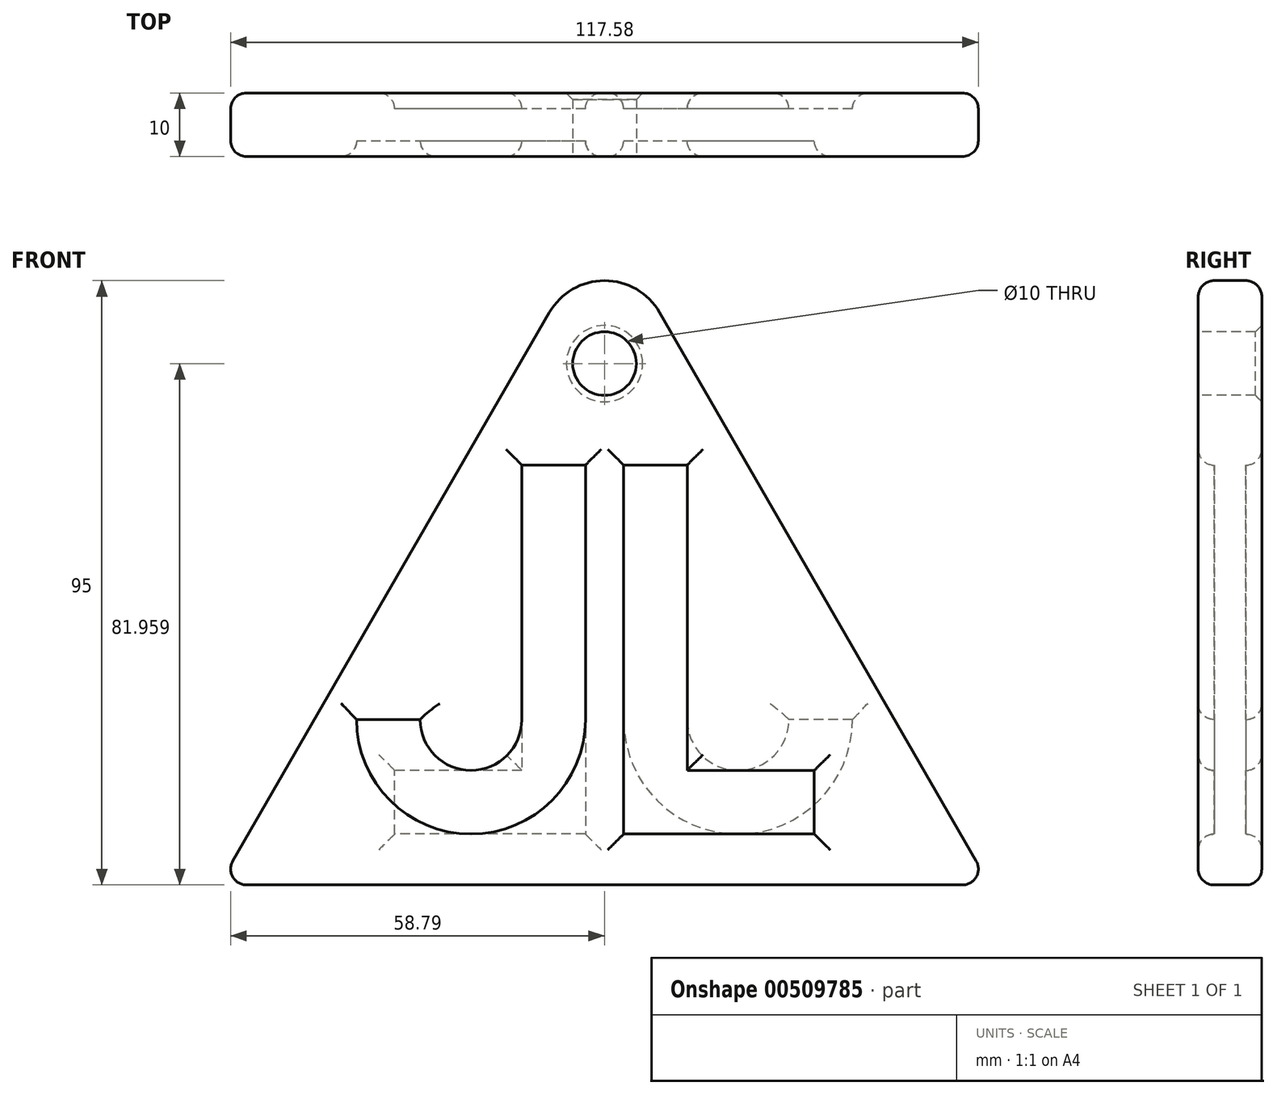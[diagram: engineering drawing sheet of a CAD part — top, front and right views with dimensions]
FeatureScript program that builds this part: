
annotation { "Feature Type Name" : "Feature", "Feature Type Description" : "" }
export const myFeature = defineFeature(function(context is Context, id is Id, definition is map)
    precondition{}
    {
        {
            var Q0;
            Q0=qCreatedBy(makeId("Front.planeOp"),FACE);
            var sketch = newSketch(context, id + "F0", { "sketchPlane" : qUnion([Q0])});
            skCircle(sketch, "E0.cCircle", {"center": v(0, 0) * mm, "radius": 35 * mm, "construction": true});
            skLineSegment(sketch, "E0.0", {"start": v(0, 70) * mm, "end": v(60.62, -35) * mm});
            skLineSegment(sketch, "E0.1", {"start": v(60.62, -35) * mm, "end": v(-60.62, -35) * mm});
            skLineSegment(sketch, "E0.2", {"start": v(-60.62, -35) * mm, "end": v(0, 70) * mm});
            skPoint(sketch, "E0.0.midPoint", {"position": v(30.31, 17.5) * mm});
            skSolve(sketch);
        }
        {
            var Q0;
            Q0=qCreatedBy(makeId("Front.planeOp"),FACE);
            var sketch = newSketch(context, id + "F1", { "sketchPlane" : qUnion([Q0])});
            skLineSegment(sketch, "E1.left", {"start": v(-3, -9) * mm, "end": v(-3, 31) * mm});
            skArc(sketch, "E2", {"start": v(-3, -9) * mm, "mid": v(-21, -27) * mm, "end": v(-39, -9) * mm});
            skArc(sketch, "E3", {"start": v(-13, -9) * mm, "mid": v(-21, -17) * mm, "end": v(-29, -9) * mm});
            skLineSegment(sketch, "E4.top", {"start": v(-13, 31) * mm, "end": v(-3, 31) * mm});
            skLineSegment(sketch, "E4.left", {"start": v(-13, -9) * mm, "end": v(-13, 31) * mm});
            skLineSegment(sketch, "E5", {"start": v(-39, -9) * mm, "end": v(-29, -9) * mm});
            skLineSegment(sketch, "E6.bottom", {"start": v(3, 31) * mm, "end": v(13, 31) * mm});
            skLineSegment(sketch, "E6.top", {"start": v(3, -27) * mm, "end": v(13, -27) * mm});
            skLineSegment(sketch, "E6.left", {"start": v(3, 31) * mm, "end": v(3, -27) * mm});
            skLineSegment(sketch, "E6.right", {"start": v(13, 31) * mm, "end": v(13, -27) * mm});
            skLineSegment(sketch, "E7.bottom", {"start": v(13, -27) * mm, "end": v(33, -27) * mm});
            skLineSegment(sketch, "E7.top", {"start": v(13, -17) * mm, "end": v(33, -17) * mm});
            skLineSegment(sketch, "E7.left", {"start": v(13, -27) * mm, "end": v(13, -17) * mm});
            skLineSegment(sketch, "E7.right", {"start": v(33, -27) * mm, "end": v(33, -17) * mm});
            skSolve(sketch);
        }
        {
            var Q0;
            Q0 = qSketchRegion(id + "F0", true);
            extrude(context, id + "F2", {"entities" : qUnion([Q0]), "depth" : 10 * mm});
        }
        {
            var Q0;
            Q0 = qSketchRegion(id + "F1", true);
            extrude(context, id + "F3", {"entities" : qUnion([Q0]), "operationType" : NewBodyOperationType.REMOVE, "depth" : 25 * mm, "hasSecondDirection" : true, "secondDirectionOppositeDirection" : false, "secondDirectionDepth" : 7.5 * mm});
        }
        {
            var Q0;
            Q0=makeQuery(id+"F2.opExtrude","CAP_FACE",FACE,{"disambiguationData":[OSD([sQuery(id+"F0.wireOp",EDGE,"E0.0"),sQuery(id+"F0.wireOp",EDGE,"E0.1"),sQuery(id+"F0.wireOp",EDGE,"E0.2")])],"isStart":true});
            var sketch = newSketch(context, id + "F4", { "sketchPlane" : qUnion([Q0])});
            skLineSegment(sketch, "E8.left", {"start": v(-3, -9) * mm, "end": v(-3, 31) * mm});
            skArc(sketch, "E9", {"start": v(-3, -9) * mm, "mid": v(-21, -27) * mm, "end": v(-39, -9) * mm});
            skArc(sketch, "E10", {"start": v(-13, -9) * mm, "mid": v(-21, -17) * mm, "end": v(-29, -9) * mm});
            skLineSegment(sketch, "E11.top", {"start": v(-13, 31) * mm, "end": v(-3, 31) * mm});
            skLineSegment(sketch, "E11.left", {"start": v(-13, -9) * mm, "end": v(-13, 31) * mm});
            skLineSegment(sketch, "E12", {"start": v(-39, -9) * mm, "end": v(-29, -9) * mm});
            skLineSegment(sketch, "E13.bottom", {"start": v(3, 31) * mm, "end": v(13, 31) * mm});
            skLineSegment(sketch, "E13.top", {"start": v(3, -27) * mm, "end": v(13, -27) * mm});
            skLineSegment(sketch, "E13.left", {"start": v(3, 31) * mm, "end": v(3, -27) * mm});
            skLineSegment(sketch, "E13.right", {"start": v(13, 31) * mm, "end": v(13, -27) * mm});
            skLineSegment(sketch, "E14.bottom", {"start": v(13, -27) * mm, "end": v(33, -27) * mm});
            skLineSegment(sketch, "E14.top", {"start": v(13, -17) * mm, "end": v(33, -17) * mm});
            skLineSegment(sketch, "E14.left", {"start": v(13, -27) * mm, "end": v(13, -17) * mm});
            skLineSegment(sketch, "E14.right", {"start": v(33, -27) * mm, "end": v(33, -17) * mm});
            skSolve(sketch);
        }
        {
            var Q0;
            Q0 = qSketchRegion(id + "F4", true);
            extrude(context, id + "F5", {"entities" : qUnion([Q0]), "operationType" : NewBodyOperationType.REMOVE, "oppositeDirection" : true, "depth" : 2.5 * mm});
        }
        {
            var Q0;
            Q0=makeQuery(id+"F2.opExtrude","SWEPT_EDGE",EDGE,{"disambiguationData":[OSD([sQuery(id+"F0.wireOp",EDGE,"E0.0"),sQuery(id+"F0.wireOp",EDGE,"E0.1")])]});
            var Q1;
            Q1=makeQuery(id+"F2.opExtrude","CAP_FACE",FACE,{"disambiguationData":[OSD([sQuery(id+"F0.wireOp",EDGE,"E0.0"),sQuery(id+"F0.wireOp",EDGE,"E0.1"),sQuery(id+"F0.wireOp",EDGE,"E0.2")])],"isStart":true});
            var Q2;
            Q2=makeQuery(id+"F2.opExtrude","SWEPT_EDGE",EDGE,{"disambiguationData":[OSD([sQuery(id+"F0.wireOp",EDGE,"E0.1"),sQuery(id+"F0.wireOp",EDGE,"E0.2")])]});
            var Q3;
            Q3=makeQuery(id+"F2.opExtrude","CAP_FACE",FACE,{"disambiguationData":[OSD([sQuery(id+"F0.wireOp",EDGE,"E0.0"),sQuery(id+"F0.wireOp",EDGE,"E0.1"),sQuery(id+"F0.wireOp",EDGE,"E0.2")])],"isStart":false});
            fillet(context, id + "F6", {"entities" : qUnion([Q0, Q1, Q2, Q3]), "radius" : 2.5 * mm, "tangentPropagation" : true, "allowEdgeOverflow" : false});
        }
        {
            var Q0;
            Q0=makeQuery(id+"F2.opExtrude","CAP_FACE",FACE,{"disambiguationData":[OSD([sQuery(id+"F0.wireOp",EDGE,"E0.0"),sQuery(id+"F0.wireOp",EDGE,"E0.1"),sQuery(id+"F0.wireOp",EDGE,"E0.2")])],"isStart":false});
            var sketch = newSketch(context, id + "F7", { "sketchPlane" : qUnion([Q0])});
            skCircle(sketch, "E15", {"center": v(0, 46.96) * mm, "radius": 5 * mm});
            skSolve(sketch);
        }
        {
            var Q0;
            Q0=makeQuery(id+"F7.imprint","IMPRINT",FACE,{"disambiguationData":[TD([[makeQuery(id+"F7.imprint","IMPRINT",EDGE,{"derivedFrom":sQuery(id+"F7.wireOp",EDGE,"E15")}),1.0]])]});
            extrude(context, id + "F8", {"entities" : qUnion([Q0]), "operationType" : NewBodyOperationType.REMOVE, "oppositeDirection" : true, "depth" : 25 * mm});
        }
        {
            var Q0;
            Q0=makeQuery(id+"F8.boolean.opBoolean","COPY",EDGE,{"derivedFrom":makeQuery(id+"F8.opExtrude","CAP_EDGE",EDGE,{"disambiguationData":[OSD([sQuery(id+"F7.wireOp",EDGE,"E15")])],"isStart":true})});
            var Q1;
            Q1=makeQuery(id+"F8.boolean.opBoolean","INTERSECT",EDGE,{"derivedFrom":[makeQuery(id+"F2.opExtrude","CAP_FACE",FACE,{"disambiguationData":[OSD([sQuery(id+"F0.wireOp",EDGE,"E0.0"),sQuery(id+"F0.wireOp",EDGE,"E0.1"),sQuery(id+"F0.wireOp",EDGE,"E0.2")])],"isStart":true}),makeQuery(id+"F8.opExtrude","SWEPT_FACE",FACE,{"disambiguationData":[OSD([sQuery(id+"F7.wireOp",EDGE,"E15")])]})]});
            chamfer(context, id + "F9", {"entities" : qUnion([Q0, Q1]), "width" : 1 * mm, "tangentPropagation" : true});
        }
        {
            var Q0;
            Q0=makeQuery(id+"F2.opExtrude","SWEPT_EDGE",EDGE,{"disambiguationData":[OSD([sQuery(id+"F0.wireOp",EDGE,"E0.0"),sQuery(id+"F0.wireOp",EDGE,"E0.2")])]});
            fillet(context, id + "F10", {"entities" : qUnion([Q0]), "radius" : 10 * mm, "tangentPropagation" : true, "allowEdgeOverflow" : false});
        }
    });
